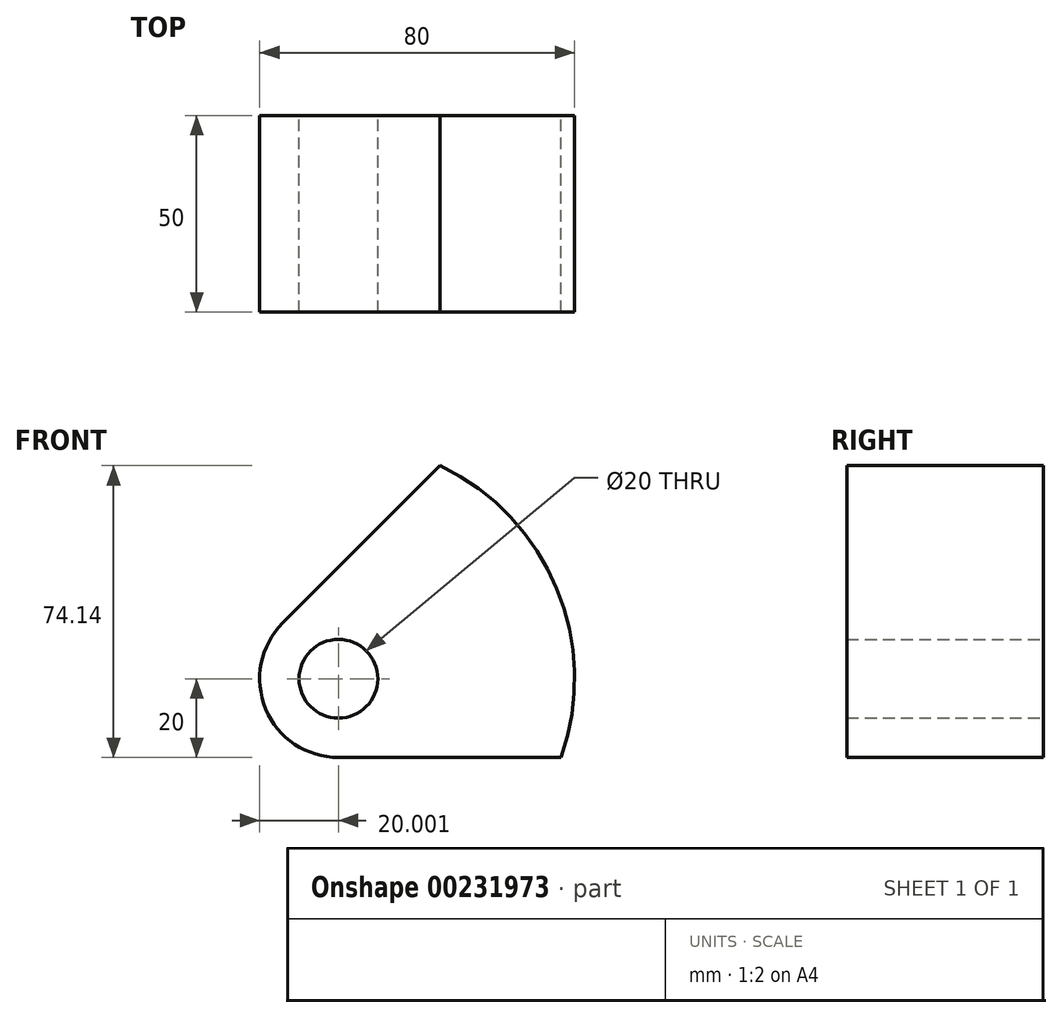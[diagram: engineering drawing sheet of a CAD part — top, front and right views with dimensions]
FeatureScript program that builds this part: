
annotation { "Feature Type Name" : "Feature", "Feature Type Description" : "" }
export const myFeature = defineFeature(function(context is Context, id is Id, definition is map)
    precondition{}
    {
        {
            var Q0;
            Q0=qCreatedBy(makeId("Front.planeOp"),FACE);
            var sketch = newSketch(context, id + "F0", { "sketchPlane" : qUnion([Q0])});
            skLineSegment(sketch, "E0", {"start": v(0, 0) * mm, "end": v(-56.57, 0) * mm});
            skArc(sketch, "E1", {"start": v(-56.57, 0) * mm, "mid": v(-75.05, 12.35) * mm, "end": v(-70.71, 34.14) * mm});
            skLineSegment(sketch, "E2", {"start": v(-70.71, 34.14) * mm, "end": v(-30.71, 74.14) * mm});
            skArc(sketch, "E3", {"start": v(0, 0) * mm, "mid": v(-1.14, 42.96) * mm, "end": v(-30.71, 74.14) * mm});
            skCircle(sketch, "E4", {"center": v(-56.57, 20) * mm, "radius": 10 * mm});
            skSolve(sketch);
        }
        {
            var Q0;
            Q0=makeQuery(id+"F0.imprint","IMPRINT",FACE,{"disambiguationData":[TD([[makeQuery(id+"F0.imprint","IMPRINT",EDGE,{"derivedFrom":sQuery(id+"F0.wireOp",EDGE,"E0")}),-1.0]])]});
            extrude(context, id + "F1", {"entities" : qUnion([Q0]), "depth" : 50 * mm});
        }
    });
